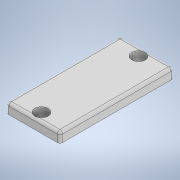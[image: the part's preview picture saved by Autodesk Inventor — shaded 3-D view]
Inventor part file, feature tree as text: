
AUTODESK INVENTOR PART (.ipt)
format: ipt  version: 2020.2 (Build 242310000, 310)  size: 128,000 bytes
history: native  units: in
note: dims shown in document units (in); Inventor stores cm internally (conversion verified against a paired STEP export)
features: sketch x2, extrude x1, hole x1, fillet x1
ambient origin geometry x8: Origin, YZ Plane, XZ Plane, XY Plane, X Axis, Y Axis, Z Axis, Center Point
bodies: Solid1 (feature_tree)
feature tree (5):
  extrude  "Extrusion1"  Depth=0.6299in
  hole  "Hole1"  [1 undecoded]
  fillet  "Fillet1"  Radius=0.0984in
  sketch  "Sketch1"  dims[d0=0.6299in d1=1.3386in]
  sketch  "Sketch2"  dims[d2=0.1181in d3=0.0in d4=0.0984in d5=0.0984in d6=0.1575in d7=0.2953in d8=0.1476in d9=0.0984in d10=90.0deg d11=0.3937in d12=0.8108in d13=0.0315in d14=0.8108in d15=0.0246in d16=0.2953in d17=0.1476in]
note: 1 required parameter value undecoded (feature->parameter linkage not recoverable at this tier; creation-order binding heuristic only, values carry confidence <= 0.55)
